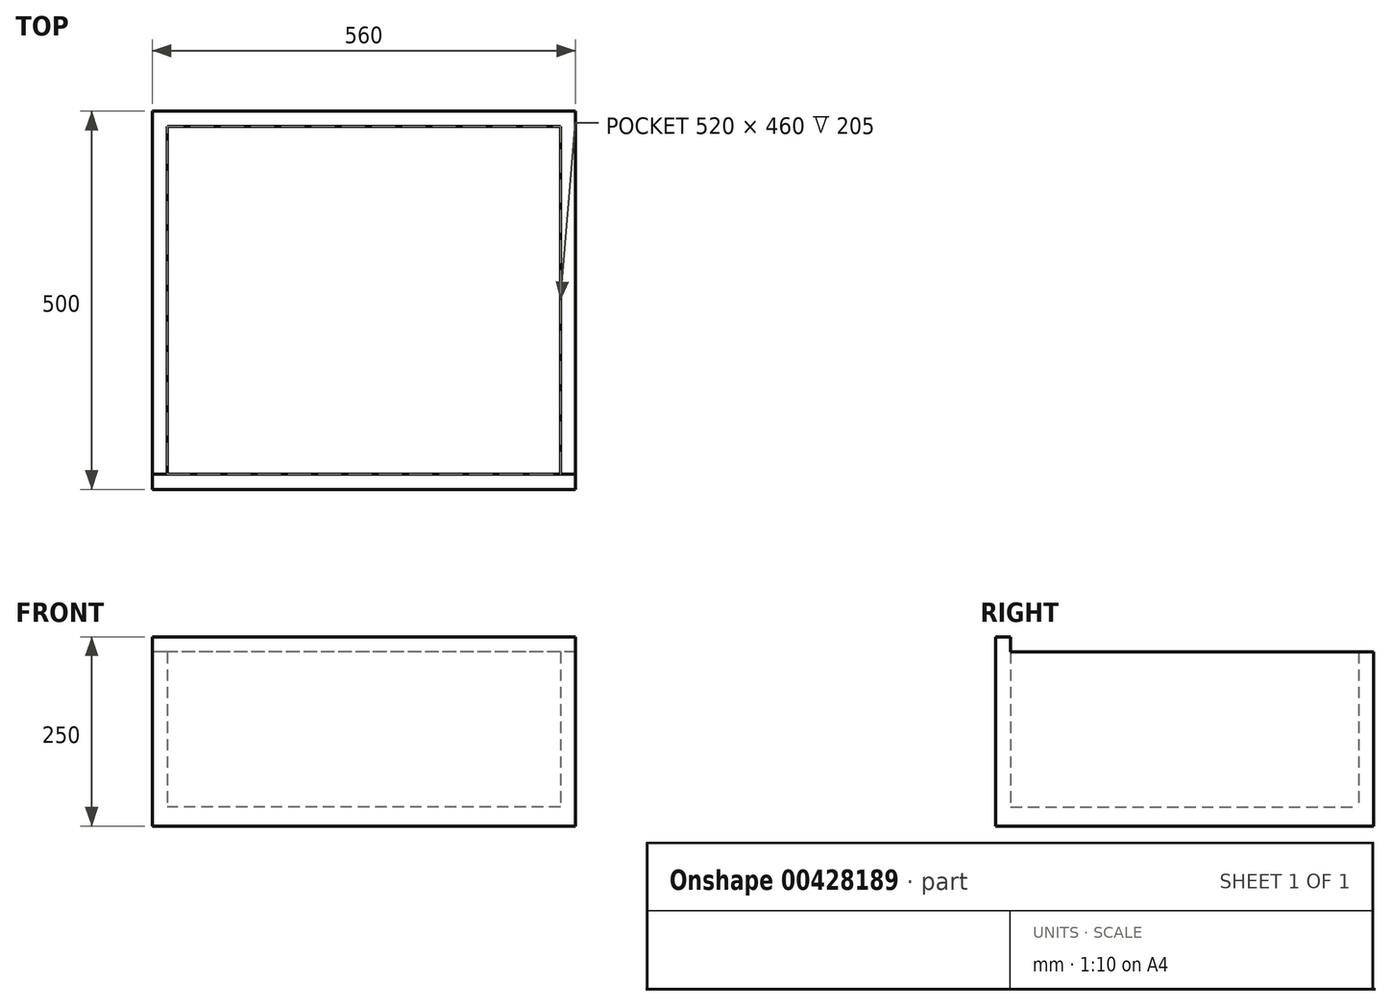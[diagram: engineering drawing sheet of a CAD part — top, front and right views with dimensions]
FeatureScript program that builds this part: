
annotation { "Feature Type Name" : "Feature", "Feature Type Description" : "" }
export const myFeature = defineFeature(function(context is Context, id is Id, definition is map)
    precondition{}
    {
        {
            var Q0;
            Q0=qCreatedBy(makeId("Top.planeOp"),FACE);
            var sketch = newSketch(context, id + "F0", { "sketchPlane" : qUnion([Q0])});
            skLineSegment(sketch, "E0.bottom", {"start": v(280, -250) * mm, "end": v(-280, -250) * mm});
            skLineSegment(sketch, "E0.top", {"start": v(280, 250) * mm, "end": v(-280, 250) * mm});
            skLineSegment(sketch, "E0.left", {"start": v(280, -250) * mm, "end": v(280, 250) * mm});
            skLineSegment(sketch, "E0.right", {"start": v(-280, -250) * mm, "end": v(-280, 250) * mm});
            skPoint(sketch, "E0.middle", {"position": v(0, 0) * mm});
            skLineSegment(sketch, "E1.0", {"start": v(-260, -250) * mm, "end": v(-260, 250) * mm});
            skLineSegment(sketch, "E2.0", {"start": v(260, -250) * mm, "end": v(260, 250) * mm});
            skLineSegment(sketch, "E3.0", {"start": v(280, 230) * mm, "end": v(-280, 230) * mm});
            skLineSegment(sketch, "E4.0", {"start": v(280, -230) * mm, "end": v(-280, -230) * mm});
            skSolve(sketch);
        }
        {
            var Q0;
            {var subQ0=sQuery(id+"F0.wireOp",EDGE,"E3.0");var subQ1=sQuery(id+"F0.wireOp",EDGE,"E0.right");var subQ2=makeQuery(id+"F0.imprint","INTERSECT",VERTEX,{"derivedFrom":[subQ1,subQ0]});Q0=makeQuery(id+"F0.imprint","IMPRINT",FACE,{"disambiguationData":[TD([[makeQuery(id+"F0.imprint","IMPRINT",EDGE,{"disambiguationData":[TD([[subQ2,1.0]])],"derivedFrom":subQ1}),-1.0]])]});}
            var Q1;
            {var subQ0=sQuery(id+"F0.wireOp",EDGE,"E0.right");var subQ1=sQuery(id+"F0.wireOp",EDGE,"E0.top");var subQ2=makeQuery(id+"F0.imprint","INTERSECT",VERTEX,{"derivedFrom":[subQ1,subQ0]});Q1=makeQuery(id+"F0.imprint","IMPRINT",FACE,{"disambiguationData":[TD([[makeQuery(id+"F0.imprint","IMPRINT",EDGE,{"disambiguationData":[TD([[subQ2,1.0]])],"derivedFrom":subQ1}),1.0]])]});}
            var Q2;
            {var subQ0=sQuery(id+"F0.wireOp",EDGE,"E1.0");var subQ1=sQuery(id+"F0.wireOp",EDGE,"E0.top");var subQ2=makeQuery(id+"F0.imprint","INTERSECT",VERTEX,{"derivedFrom":[subQ1,subQ0]});Q2=makeQuery(id+"F0.imprint","IMPRINT",FACE,{"disambiguationData":[TD([[makeQuery(id+"F0.imprint","IMPRINT",EDGE,{"disambiguationData":[TD([[subQ2,1.0]])],"derivedFrom":subQ1}),1.0]])]});}
            var Q3;
            {var subQ0=sQuery(id+"F0.wireOp",EDGE,"E3.0");var subQ1=sQuery(id+"F0.wireOp",EDGE,"E0.left");var subQ2=makeQuery(id+"F0.imprint","INTERSECT",VERTEX,{"derivedFrom":[subQ1,subQ0]});Q3=makeQuery(id+"F0.imprint","IMPRINT",FACE,{"disambiguationData":[TD([[makeQuery(id+"F0.imprint","IMPRINT",EDGE,{"disambiguationData":[TD([[subQ2,1.0]])],"derivedFrom":subQ1}),1.0]])]});}
            var Q4;
            {var subQ0=sQuery(id+"F0.wireOp",EDGE,"E0.left");var subQ1=sQuery(id+"F0.wireOp",EDGE,"E0.top");var subQ2=makeQuery(id+"F0.imprint","INTERSECT",VERTEX,{"derivedFrom":[subQ1,subQ0]});Q4=makeQuery(id+"F0.imprint","IMPRINT",FACE,{"disambiguationData":[TD([[makeQuery(id+"F0.imprint","IMPRINT",EDGE,{"disambiguationData":[TD([[subQ2,-1.0]])],"derivedFrom":subQ1}),1.0]])]});}
            extrude(context, id + "F1", {"entities" : qUnion([Q0, Q1, Q2, Q3, Q4]), "depth" : 230 * mm});
        }
        {
            var Q0;
            {var subQ0=sQuery(id+"F0.wireOp",EDGE,"E0.right");var subQ1=sQuery(id+"F0.wireOp",EDGE,"E0.bottom");var subQ2=makeQuery(id+"F0.imprint","INTERSECT",VERTEX,{"derivedFrom":[subQ1,subQ0]});Q0=makeQuery(id+"F0.imprint","IMPRINT",FACE,{"disambiguationData":[TD([[makeQuery(id+"F0.imprint","IMPRINT",EDGE,{"disambiguationData":[TD([[subQ2,1.0]])],"derivedFrom":subQ1}),-1.0]])]});}
            var Q1;
            {var subQ0=sQuery(id+"F0.wireOp",EDGE,"E1.0");var subQ1=sQuery(id+"F0.wireOp",EDGE,"E0.bottom");var subQ2=makeQuery(id+"F0.imprint","INTERSECT",VERTEX,{"derivedFrom":[subQ1,subQ0]});Q1=makeQuery(id+"F0.imprint","IMPRINT",FACE,{"disambiguationData":[TD([[makeQuery(id+"F0.imprint","IMPRINT",EDGE,{"disambiguationData":[TD([[subQ2,1.0]])],"derivedFrom":subQ1}),-1.0]])]});}
            var Q2;
            {var subQ0=sQuery(id+"F0.wireOp",EDGE,"E0.left");var subQ1=sQuery(id+"F0.wireOp",EDGE,"E0.bottom");var subQ2=makeQuery(id+"F0.imprint","INTERSECT",VERTEX,{"derivedFrom":[subQ1,subQ0]});Q2=makeQuery(id+"F0.imprint","IMPRINT",FACE,{"disambiguationData":[TD([[makeQuery(id+"F0.imprint","IMPRINT",EDGE,{"disambiguationData":[TD([[subQ2,-1.0]])],"derivedFrom":subQ1}),-1.0]])]});}
            extrude(context, id + "F2", {"entities" : qUnion([Q0, Q1, Q2]), "operationType" : NewBodyOperationType.ADD, "depth" : 250 * mm});
        }
        {
            var Q0;
            Q0 = qSketchRegion(id + "F0", true);
            var Q1;
            {var subQ0=sQuery(id+"F0.wireOp",EDGE,"E4.0");var subQ1=sQuery(id+"F0.wireOp",EDGE,"E1.0");var subQ2=makeQuery(id+"F0.imprint","INTERSECT",VERTEX,{"derivedFrom":[subQ1,subQ0]});Q1=makeQuery(id+"F0.imprint","IMPRINT",FACE,{"disambiguationData":[TD([[makeQuery(id+"F0.imprint","IMPRINT",EDGE,{"disambiguationData":[TD([[subQ2,-1.0]])],"derivedFrom":subQ1}),-1.0]])]});}
            extrude(context, id + "F3", {"entities" : qUnion([Q0, Q1]), "operationType" : NewBodyOperationType.ADD, "depth" : 25 * mm});
        }
    });
